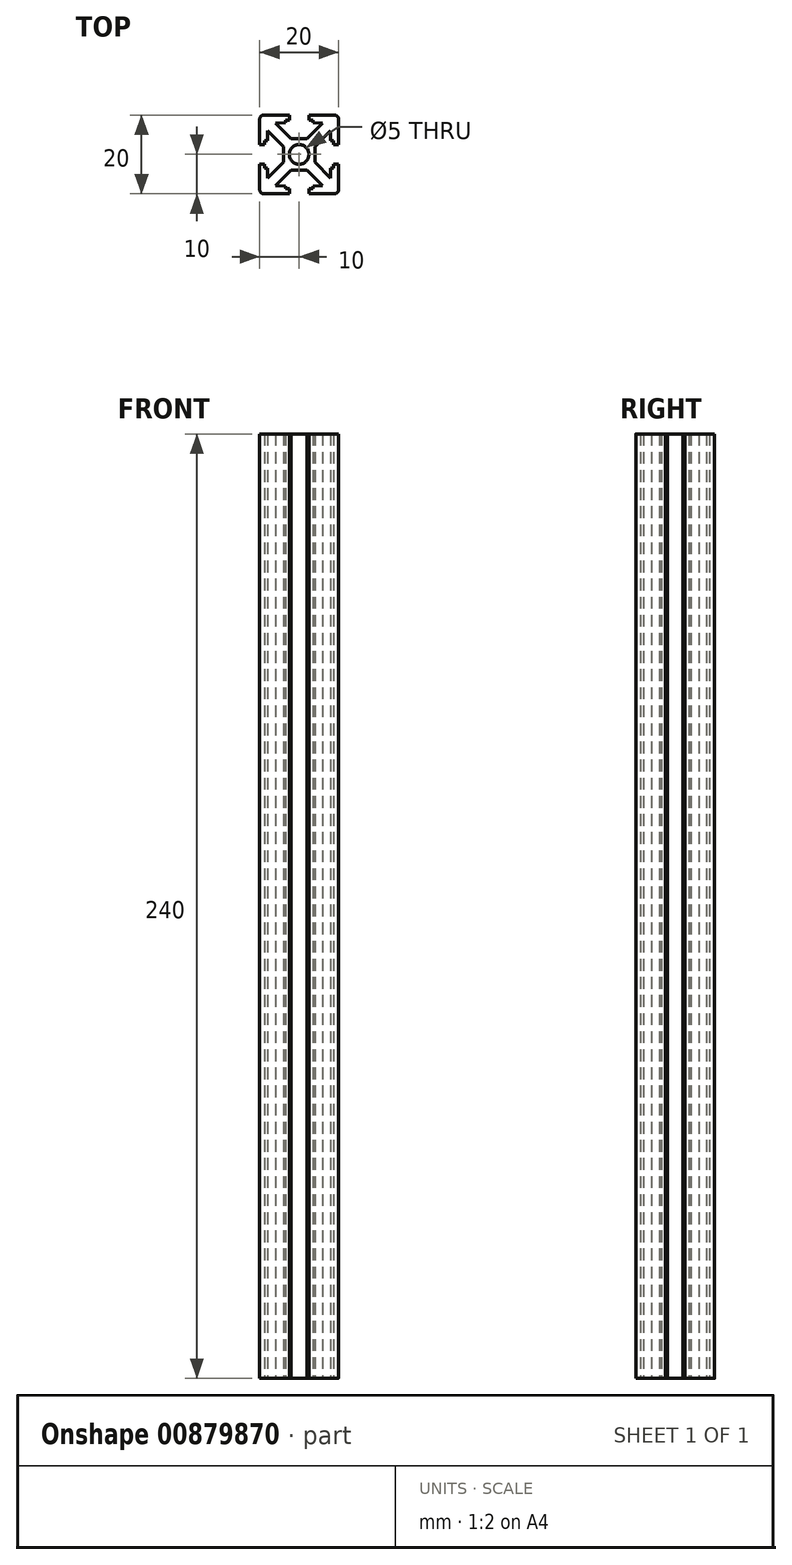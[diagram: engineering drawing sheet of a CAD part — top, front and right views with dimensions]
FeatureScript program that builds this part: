
annotation { "Feature Type Name" : "Feature", "Feature Type Description" : "" }
export const myFeature = defineFeature(function(context is Context, id is Id, definition is map)
    precondition{}
    {
        {
            var Q0;
            Q0=qCreatedBy(makeId("Top.planeOp"),FACE);
            var sketch = newSketch(context, id + "F0", { "sketchPlane" : qUnion([Q0])});
            skLineSegment(sketch, "E0.bottom", {"start": v(-2, 4) * mm, "end": v(0, 4) * mm});
            skLineSegment(sketch, "E0.left", {"start": v(-4, 2) * mm, "end": v(-4, 0) * mm});
            skLineSegment(sketch, "E1.top", {"start": v(-10, 2.5) * mm, "end": v(-8.75, 2.5) * mm});
            skLineSegment(sketch, "E2.trimOffspring", {"start": v(-8, 6) * mm, "end": v(-8, 3.5) * mm});
            skLineSegment(sketch, "E3", {"start": v(-6, 8) * mm, "end": v(-2, 4) * mm});
            skLineSegment(sketch, "E4", {"start": v(-8, 6) * mm, "end": v(-4, 2) * mm});
            skLineSegment(sketch, "E5.right", {"start": v(-3.5, 8) * mm, "end": v(-3.5, 8.75) * mm});
            skLineSegment(sketch, "E6.right", {"start": v(-2.5, 8.75) * mm, "end": v(-2.5, 10) * mm});
            skLineSegment(sketch, "E7", {"start": v(-3.5, 8.75) * mm, "end": v(-2.5, 8.75) * mm});
            skLineSegment(sketch, "E8", {"start": v(-10, 10) * mm, "end": v(-2.5, 10) * mm});
            skLineSegment(sketch, "E9.top", {"start": v(-8, 3.5) * mm, "end": v(-8.75, 3.5) * mm});
            skLineSegment(sketch, "E9.right", {"start": v(-8.75, 2.5) * mm, "end": v(-8.75, 3.5) * mm});
            skLineSegment(sketch, "E10", {"start": v(-10, 10) * mm, "end": v(-10, 2.5) * mm});
            skLineSegment(sketch, "E11", {"start": v(-6, 8) * mm, "end": v(-3.5, 8) * mm});
            skLineSegment(sketch, "E12.MirrorCS", {"start": v(3.5, 8) * mm, "end": v(3.5, 8.75) * mm});
            skLineSegment(sketch, "E13.MirrorCS", {"start": v(4, 2) * mm, "end": v(4, 0) * mm});
            skLineSegment(sketch, "E14.MirrorCS", {"start": v(8, 3.5) * mm, "end": v(8.75, 3.5) * mm});
            skLineSegment(sketch, "E15.MirrorCS", {"start": v(8, 6) * mm, "end": v(8, 3.5) * mm});
            skLineSegment(sketch, "E16.MirrorCS", {"start": v(2, 4) * mm, "end": v(0, 4) * mm});
            skLineSegment(sketch, "E17.MirrorCS", {"start": v(10, 2.5) * mm, "end": v(8.75, 2.5) * mm});
            skLineSegment(sketch, "E18.MirrorCS", {"start": v(6, 8) * mm, "end": v(2, 4) * mm});
            skLineSegment(sketch, "E19.MirrorCS", {"start": v(2.5, 8.75) * mm, "end": v(2.5, 10) * mm});
            skLineSegment(sketch, "E20.MirrorCS", {"start": v(6, 8) * mm, "end": v(3.5, 8) * mm});
            skLineSegment(sketch, "E21.MirrorCS", {"start": v(8.75, 2.5) * mm, "end": v(8.75, 3.5) * mm});
            skLineSegment(sketch, "E22.MirrorCS", {"start": v(10, 10) * mm, "end": v(10, 2.5) * mm});
            skLineSegment(sketch, "E23.MirrorCS", {"start": v(10, 10) * mm, "end": v(2.5, 10) * mm});
            skLineSegment(sketch, "E24.MirrorCS", {"start": v(8, 6) * mm, "end": v(4, 2) * mm});
            skLineSegment(sketch, "E25.MirrorCS", {"start": v(3.5, 8.75) * mm, "end": v(2.5, 8.75) * mm});
            skLineSegment(sketch, "E26.MirrorCS", {"start": v(-3.5, -8) * mm, "end": v(-3.5, -8.75) * mm});
            skLineSegment(sketch, "E27.MirrorCS", {"start": v(-8, -3.5) * mm, "end": v(-8.75, -3.5) * mm});
            skLineSegment(sketch, "E28.MirrorCS", {"start": v(8, -3.5) * mm, "end": v(8.75, -3.5) * mm});
            skLineSegment(sketch, "E29.MirrorCS", {"start": v(-8.75, -2.5) * mm, "end": v(-8.75, -3.5) * mm});
            skLineSegment(sketch, "E30.MirrorCS", {"start": v(3.5, -8) * mm, "end": v(3.5, -8.75) * mm});
            skLineSegment(sketch, "E31.MirrorCS", {"start": v(-8, -6) * mm, "end": v(-4, -2) * mm});
            skLineSegment(sketch, "E32.MirrorCS", {"start": v(8.75, -2.5) * mm, "end": v(8.75, -3.5) * mm});
            skLineSegment(sketch, "E33.MirrorCS", {"start": v(-2, -4) * mm, "end": v(0, -4) * mm});
            skLineSegment(sketch, "E34.MirrorCS", {"start": v(-6, -8) * mm, "end": v(-2, -4) * mm});
            skLineSegment(sketch, "E35.MirrorCS", {"start": v(10, -2.5) * mm, "end": v(8.75, -2.5) * mm});
            skLineSegment(sketch, "E36.MirrorCS", {"start": v(-3.5, -8.75) * mm, "end": v(-2.5, -8.75) * mm});
            skLineSegment(sketch, "E37.MirrorCS", {"start": v(6, -8) * mm, "end": v(3.5, -8) * mm});
            skLineSegment(sketch, "E38.MirrorCS", {"start": v(-2.5, -8.75) * mm, "end": v(-2.5, -10) * mm});
            skLineSegment(sketch, "E39.MirrorCS", {"start": v(-6, -8) * mm, "end": v(-3.5, -8) * mm});
            skLineSegment(sketch, "E40.MirrorCS", {"start": v(10, -10) * mm, "end": v(2.5, -10) * mm});
            skLineSegment(sketch, "E41.MirrorCS", {"start": v(-10, -10) * mm, "end": v(-10, -2.5) * mm});
            skLineSegment(sketch, "E42.MirrorCS", {"start": v(3.5, -8.75) * mm, "end": v(2.5, -8.75) * mm});
            skLineSegment(sketch, "E43.MirrorCS", {"start": v(-10, -10) * mm, "end": v(-2.5, -10) * mm});
            skLineSegment(sketch, "E44.MirrorCS", {"start": v(4, -2) * mm, "end": v(4, 0) * mm});
            skLineSegment(sketch, "E45.MirrorCS", {"start": v(2.5, -8.75) * mm, "end": v(2.5, -10) * mm});
            skLineSegment(sketch, "E46.MirrorCS", {"start": v(8, -6) * mm, "end": v(8, -3.5) * mm});
            skLineSegment(sketch, "E47.MirrorCS", {"start": v(-4, -2) * mm, "end": v(-4, 0) * mm});
            skLineSegment(sketch, "E48.MirrorCS", {"start": v(6, -8) * mm, "end": v(2, -4) * mm});
            skLineSegment(sketch, "E49.MirrorCS", {"start": v(10, -10) * mm, "end": v(10, -2.5) * mm});
            skLineSegment(sketch, "E50.MirrorCS", {"start": v(8, -6) * mm, "end": v(4, -2) * mm});
            skLineSegment(sketch, "E51.MirrorCS", {"start": v(2, -4) * mm, "end": v(0, -4) * mm});
            skLineSegment(sketch, "E52.MirrorCS", {"start": v(-8, -6) * mm, "end": v(-8, -3.5) * mm});
            skLineSegment(sketch, "E53.MirrorCS", {"start": v(-10, -2.5) * mm, "end": v(-8.75, -2.5) * mm});
            skLineSegment(sketch, "E54", {"start": v(-3.5, 8.75) * mm, "end": v(-3.5, 5.5) * mm, "construction": true});
            skLineSegment(sketch, "E55", {"start": v(-3.5, 5.5) * mm, "end": v(3.5, 5.5) * mm, "construction": true});
            skLineSegment(sketch, "E56", {"start": v(-2.5, 8.75) * mm, "end": v(2.5, 8.75) * mm, "construction": true});
            skSolve(sketch);
        }
        {
            var Q0;
            Q0=makeQuery(id+"F0.imprint","IMPRINT",FACE,{"disambiguationData":[TD([[makeQuery(id+"F0.imprint","IMPRINT",EDGE,{"derivedFrom":sQuery(id+"F0.wireOp",EDGE,"E0.bottom")}),-1.0]])]});
            extrude(context, id + "F1", {"entities" : qUnion([Q0]), "depth" : 240 * mm, "offsetDistance" : 25 * mm});
        }
        {
            var Q0;
            Q0=makeQuery(id+"F1.opExtrude","SWEPT_EDGE",EDGE,{"disambiguationData":[OSD([sQuery(id+"F0.wireOp",EDGE,"E41.MirrorCS"),sQuery(id+"F0.wireOp",EDGE,"E43.MirrorCS")])]});
            var Q1;
            Q1=makeQuery(id+"F1.opExtrude","SWEPT_EDGE",EDGE,{"disambiguationData":[OSD([sQuery(id+"F0.wireOp",EDGE,"E40.MirrorCS"),sQuery(id+"F0.wireOp",EDGE,"E49.MirrorCS")])]});
            var Q2;
            Q2=makeQuery(id+"F1.opExtrude","SWEPT_EDGE",EDGE,{"disambiguationData":[OSD([sQuery(id+"F0.wireOp",EDGE,"E8"),sQuery(id+"F0.wireOp",EDGE,"E10")])]});
            var Q3;
            Q3=makeQuery(id+"F1.opExtrude","SWEPT_EDGE",EDGE,{"disambiguationData":[OSD([sQuery(id+"F0.wireOp",EDGE,"E22.MirrorCS"),sQuery(id+"F0.wireOp",EDGE,"E23.MirrorCS")])]});
            fillet(context, id + "F2", {"entities" : qUnion([Q0, Q1, Q2, Q3]), "radius" : 1 * mm, "tangentPropagation" : true, "allowEdgeOverflow" : false});
        }
        {
            var Q0;
            Q0=makeQuery(id+"F1.opExtrude","CAP_FACE",FACE,{"disambiguationData":[OSD([sQuery(id+"F0.wireOp",EDGE,"E0.bottom"),sQuery(id+"F0.wireOp",EDGE,"E0.top"),sQuery(id+"F0.wireOp",EDGE,"E0.left"),sQuery(id+"F0.wireOp",EDGE,"E0.right"),sQuery(id+"F0.wireOp",EDGE,"E1.top"),sQuery(id+"F0.wireOp",EDGE,"E1.left"),sQuery(id+"F0.wireOp",EDGE,"7sOvannw-PQdt-Ueeu-KgLe-8v3CC9pdS52h.bottom"),sQuery(id+"F0.wireOp",EDGE,"7sOvannw-PQdt-Ueeu-KgLe-8v3CC9pdS52h.top"),sQuery(id+"F0.wireOp",EDGE,"7sOvannw-PQdt-Ueeu-KgLe-8v3CC9pdS52h.left"),sQuery(id+"F0.wireOp",EDGE,"7sOvannw-PQdt-Ueeu-KgLe-8v3CC9pdS52h.right"),sQuery(id+"F0.wireOp",EDGE,"E2.trimOffspring"),sQuery(id+"F0.wireOp",EDGE,"E3"),sQuery(id+"F0.wireOp",EDGE,"E4"),sQuery(id+"F0.wireOp",EDGE,"71accefe-0b79-4fcc-9481-b649415a30997.MirrorCS"),sQuery(id+"F0.wireOp",EDGE,"71accefe-0b79-4fcc-9481-b649415a30998.MirrorCS"),sQuery(id+"F0.wireOp",EDGE,"71accefe-0b79-4fcc-9481-b649415a30999.MirrorCS"),sQuery(id+"F0.wireOp",EDGE,"71accefe-0b79-4fcc-9481-b649415a309912.MirrorCS"),sQuery(id+"F0.wireOp",EDGE,"71accefe-0b79-4fcc-9481-b649415a309914.MirrorCS"),sQuery(id+"F0.wireOp",EDGE,"71accefe-0b79-4fcc-9481-b649415a309916.MirrorCS"),sQuery(id+"F0.wireOp",EDGE,"71accefe-0b79-4fcc-9481-b649415a309917.MirrorCS"),sQuery(id+"F0.wireOp",EDGE,"71accefe-0b79-4fcc-9481-b649415a309919.MirrorCS"),sQuery(id+"F0.wireOp",EDGE,"b965ea24-d8d2-4ec5-b2df-8227e64444407.MirrorCS"),sQuery(id+"F0.wireOp",EDGE,"b965ea24-d8d2-4ec5-b2df-8227e644444011.MirrorCS"),sQuery(id+"F0.wireOp",EDGE,"b965ea24-d8d2-4ec5-b2df-8227e644444012.MirrorCS"),sQuery(id+"F0.wireOp",EDGE,"b965ea24-d8d2-4ec5-b2df-8227e644444016.MirrorCS"),sQuery(id+"F0.wireOp",EDGE,"b965ea24-d8d2-4ec5-b2df-8227e644444017.MirrorCS"),sQuery(id+"F0.wireOp",EDGE,"b965ea24-d8d2-4ec5-b2df-8227e644444018.MirrorCS"),sQuery(id+"F0.wireOp",EDGE,"b965ea24-d8d2-4ec5-b2df-8227e644444020.MirrorCS"),sQuery(id+"F0.wireOp",EDGE,"b965ea24-d8d2-4ec5-b2df-8227e644444023.MirrorCS"),sQuery(id+"F0.wireOp",EDGE,"e400384d-8a2a-42bf-8f9f-3f607a529f7d13.MirrorCS"),sQuery(id+"F0.wireOp",EDGE,"e400384d-8a2a-42bf-8f9f-3f607a529f7d14.MirrorCS"),sQuery(id+"F0.wireOp",EDGE,"e400384d-8a2a-42bf-8f9f-3f607a529f7d16.MirrorCS"),sQuery(id+"F0.wireOp",EDGE,"e400384d-8a2a-42bf-8f9f-3f607a529f7d19.MirrorCS"),sQuery(id+"F0.wireOp",EDGE,"e400384d-8a2a-42bf-8f9f-3f607a529f7d20.MirrorCS"),sQuery(id+"F0.wireOp",EDGE,"e400384d-8a2a-42bf-8f9f-3f607a529f7d21.MirrorCS"),sQuery(id+"F0.wireOp",EDGE,"e400384d-8a2a-42bf-8f9f-3f607a529f7d23.MirrorCS"),sQuery(id+"F0.wireOp",EDGE,"e400384d-8a2a-42bf-8f9f-3f607a529f7d24.MirrorCS"),sQuery(id+"F0.wireOp",EDGE,"e400384d-8a2a-42bf-8f9f-3f607a529f7d25.MirrorCS"),sQuery(id+"F0.wireOp",EDGE,"e400384d-8a2a-42bf-8f9f-3f607a529f7d26.MirrorCS")])],"isStart":true});
            var sketch = newSketch(context, id + "F3", { "sketchPlane" : qUnion([Q0])});
            skCircle(sketch, "E57", {"center": v(0, 0) * mm, "radius": 2.5 * mm});
            skSolve(sketch);
        }
        {
            var Q0;
            Q0 = qSketchRegion(id + "F3", true);
            var Q1;
            Q1=makeQuery(id+"F1.opExtrude","CAP_FACE",FACE,{"disambiguationData":[OSD([sQuery(id+"F0.wireOp",EDGE,"E0.bottom"),sQuery(id+"F0.wireOp",EDGE,"E0.top"),sQuery(id+"F0.wireOp",EDGE,"E0.left"),sQuery(id+"F0.wireOp",EDGE,"E0.right"),sQuery(id+"F0.wireOp",EDGE,"E1.top"),sQuery(id+"F0.wireOp",EDGE,"E1.left"),sQuery(id+"F0.wireOp",EDGE,"7sOvannw-PQdt-Ueeu-KgLe-8v3CC9pdS52h.bottom"),sQuery(id+"F0.wireOp",EDGE,"7sOvannw-PQdt-Ueeu-KgLe-8v3CC9pdS52h.top"),sQuery(id+"F0.wireOp",EDGE,"7sOvannw-PQdt-Ueeu-KgLe-8v3CC9pdS52h.left"),sQuery(id+"F0.wireOp",EDGE,"7sOvannw-PQdt-Ueeu-KgLe-8v3CC9pdS52h.right"),sQuery(id+"F0.wireOp",EDGE,"E2.trimOffspring"),sQuery(id+"F0.wireOp",EDGE,"E3"),sQuery(id+"F0.wireOp",EDGE,"E4"),sQuery(id+"F0.wireOp",EDGE,"71accefe-0b79-4fcc-9481-b649415a30997.MirrorCS"),sQuery(id+"F0.wireOp",EDGE,"71accefe-0b79-4fcc-9481-b649415a30998.MirrorCS"),sQuery(id+"F0.wireOp",EDGE,"71accefe-0b79-4fcc-9481-b649415a30999.MirrorCS"),sQuery(id+"F0.wireOp",EDGE,"71accefe-0b79-4fcc-9481-b649415a309912.MirrorCS"),sQuery(id+"F0.wireOp",EDGE,"71accefe-0b79-4fcc-9481-b649415a309914.MirrorCS"),sQuery(id+"F0.wireOp",EDGE,"71accefe-0b79-4fcc-9481-b649415a309916.MirrorCS"),sQuery(id+"F0.wireOp",EDGE,"71accefe-0b79-4fcc-9481-b649415a309917.MirrorCS"),sQuery(id+"F0.wireOp",EDGE,"71accefe-0b79-4fcc-9481-b649415a309919.MirrorCS"),sQuery(id+"F0.wireOp",EDGE,"b965ea24-d8d2-4ec5-b2df-8227e64444407.MirrorCS"),sQuery(id+"F0.wireOp",EDGE,"b965ea24-d8d2-4ec5-b2df-8227e644444011.MirrorCS"),sQuery(id+"F0.wireOp",EDGE,"b965ea24-d8d2-4ec5-b2df-8227e644444012.MirrorCS"),sQuery(id+"F0.wireOp",EDGE,"b965ea24-d8d2-4ec5-b2df-8227e644444016.MirrorCS"),sQuery(id+"F0.wireOp",EDGE,"b965ea24-d8d2-4ec5-b2df-8227e644444017.MirrorCS"),sQuery(id+"F0.wireOp",EDGE,"b965ea24-d8d2-4ec5-b2df-8227e644444018.MirrorCS"),sQuery(id+"F0.wireOp",EDGE,"b965ea24-d8d2-4ec5-b2df-8227e644444020.MirrorCS"),sQuery(id+"F0.wireOp",EDGE,"b965ea24-d8d2-4ec5-b2df-8227e644444023.MirrorCS"),sQuery(id+"F0.wireOp",EDGE,"e400384d-8a2a-42bf-8f9f-3f607a529f7d13.MirrorCS"),sQuery(id+"F0.wireOp",EDGE,"e400384d-8a2a-42bf-8f9f-3f607a529f7d14.MirrorCS"),sQuery(id+"F0.wireOp",EDGE,"e400384d-8a2a-42bf-8f9f-3f607a529f7d16.MirrorCS"),sQuery(id+"F0.wireOp",EDGE,"e400384d-8a2a-42bf-8f9f-3f607a529f7d19.MirrorCS"),sQuery(id+"F0.wireOp",EDGE,"e400384d-8a2a-42bf-8f9f-3f607a529f7d20.MirrorCS"),sQuery(id+"F0.wireOp",EDGE,"e400384d-8a2a-42bf-8f9f-3f607a529f7d21.MirrorCS"),sQuery(id+"F0.wireOp",EDGE,"e400384d-8a2a-42bf-8f9f-3f607a529f7d23.MirrorCS"),sQuery(id+"F0.wireOp",EDGE,"e400384d-8a2a-42bf-8f9f-3f607a529f7d24.MirrorCS"),sQuery(id+"F0.wireOp",EDGE,"e400384d-8a2a-42bf-8f9f-3f607a529f7d25.MirrorCS"),sQuery(id+"F0.wireOp",EDGE,"e400384d-8a2a-42bf-8f9f-3f607a529f7d26.MirrorCS")])],"isStart":false});
            extrude(context, id + "F4", {"entities" : qUnion([Q0]), "operationType" : NewBodyOperationType.REMOVE, "endBound" : BoundingType.UP_TO_SURFACE, "oppositeDirection" : true, "depth" : 25 * mm, "endBoundEntityFace" : qUnion([Q1]), "offsetDistance" : 25 * mm});
        }
    });
